FCSTD DOCUMENT  (FreeCAD 1.0R39109 (Git))
Label: splitflap
License: All rights reserved
LicenseURL: https://en.wikipedia.org/wiki/All_rights_reserved
objects: App::Link×18, App::FeaturePython×13, Assembly::AssemblyLink×1, Assembly::JointGroup×1, Assembly::AssemblyObject×1
EXTERNAL_REF file=front.FCStd obj=Body
EXTERNAL_REF file=sideLeft.FCStd obj=Body
EXTERNAL_REF file=sideMotor.FCStd obj=Body
EXTERNAL_REF file=bodySpacer.FCStd obj=Body
EXTERNAL_REF file=hardware/17HS13-0404D.FCStd obj=Part__Feature
EXTERNAL_REF file=motorSpacer.FCStd obj=Body
EXTERNAL_REF file=barrel/barrel.FCStd obj=Assembly
EXTERNAL_REF file=barrel/barrel.FCStd obj=Body
EXTERNAL_REF file=barrel/barrel.FCStd obj=Body001
EXTERNAL_REF file=barrel/barrel.FCStd obj=Body002
EXTERNAL_REF file=barrel/barrel.FCStd obj=Body003
EXTERNAL_REF file=barrel/barrel.FCStd obj=Body004
EXTERNAL_REF file=barrel/barrel.FCStd obj=Body007
EXTERNAL_REF file=barrel/barrel.FCStd obj=Body008
EXTERNAL_REF file=barrel/barrel.FCStd obj=Body009

FEATURE [App::Link] Body  label="Front"
  LinkPlacement = pos=(3.15e-14,-7,0) rot=(0,0,1;0rad)
  LinkedObject = -> <external front.FCStd>#Body
  Placement = pos=(3.15e-14,-7,0) rot=(0,0,1;0rad)
FEATURE [App::Link] Body006  label="LeftSide"
  LinkPlacement = pos=(36,-7,-80) rot=(0,0,1;0rad)
  LinkedObject = -> <external sideLeft.FCStd>#Body
  Placement = pos=(36,-7,-80) rot=(0,0,1;0rad)
FEATURE [App::Link] Body007  label="RightSide"
  LinkPlacement = pos=(-40,-7,-80) rot=(0,0,1;0rad)
  LinkedObject = -> <external sideMotor.FCStd>#Body
  Placement = pos=(-40,-7,-80) rot=(0,0,1;0rad)
FEATURE [App::Link] Body011  label="BodySpacerBottom"
  LinkPlacement = pos=(36,93,-75) rot=(0.57735,0.57735,-0.57735;4.18879rad)
  LinkedObject = -> <external bodySpacer.FCStd>#Body
  Placement = pos=(36,93,-75) rot=(0.57735,0.57735,-0.57735;4.18879rad)
FEATURE [App::Link] Body012  label="BodySpacerTop"
  LinkPlacement = pos=(36,88,70) rot=(0.57735,0.57735,-0.57735;4.18879rad)
  LinkedObject = -> <external bodySpacer.FCStd>#Body
  Placement = pos=(36,88,70) rot=(0.57735,0.57735,-0.57735;4.18879rad)
FEATURE [App::Link] _7HS13_0404D  label="17HS13-0404D"
  LinkPlacement = pos=(9,29,10) rot=(0.57735,0.57735,-0.57735;4.18879rad)
  LinkedObject = -> <external hardware/17HS13-0404D.FCStd>#Part__Feature
  Placement = pos=(9,29,10) rot=(0.57735,0.57735,-0.57735;4.18879rad)
FEATURE [App::Link] Body015  label="MotorSpacer"
  LinkPlacement = pos=(-36,13.5,-5.5) rot=(0.57735,0.57735,0.57735;2.0944rad)
  LinkedObject = -> <external motorSpacer.FCStd>#Body
  Placement = pos=(-36,13.5,-5.5) rot=(0.57735,0.57735,0.57735;2.0944rad)
FEATURE [App::Link] Body016  label="MotorSpacer001"
  LinkPlacement = pos=(-24,44.5,-5.5) rot=(0.57735,0.57735,-0.57735;4.18879rad)
  LinkedObject = -> <external motorSpacer.FCStd>#Body
  Placement = pos=(-24,44.5,-5.5) rot=(0.57735,0.57735,-0.57735;4.18879rad)
FEATURE [App::Link] Body017  label="MotorSpacer002"
  LinkPlacement = pos=(-24,44.5,25.5) rot=(-0.57735,-0.57735,0.57735;2.0944rad)
  LinkedObject = -> <external motorSpacer.FCStd>#Body
  Placement = pos=(-24,44.5,25.5) rot=(-0.57735,-0.57735,0.57735;2.0944rad)
FEATURE [App::Link] Body018  label="MotorSpacer003"
  LinkPlacement = pos=(-36,13.5,25.5) rot=(0.57735,0.57735,0.57735;2.0944rad)
  LinkedObject = -> <external motorSpacer.FCStd>#Body
  Placement = pos=(-36,13.5,25.5) rot=(0.57735,0.57735,0.57735;2.0944rad)
FEATURE [App::FeaturePython] GroundedJoint  # Assembly grounded joint (typed FeaturePython)
  ObjectToGround = -> Body
  Placement = pos=(3.15e-14,-7,0) rot=(0,0,1;0rad)
FEATURE [App::FeaturePython] Joint  label="FrontLeftTop"  # Assembly joint (typed FeaturePython)
  Activated = true
  AngleMax = 0
  AngleMin = 0
  Detach1 = false
  Detach2 = false
  Distance = 0
  Distance2 = 0
  EnableAngleMax = false
  EnableAngleMin = false
  EnableLengthMax = false
  EnableLengthMin = false
  JointType = 0 (Fixed)
  LengthMax = 0
  LengthMin = 0
  Offset2 = pos=(0,0,0) rot=(0,0,-1;1.5708rad)
  Placement1 = pos=(4,5,155) rot=(0.57735,0.57735,0.57735;2.0944rad)
  Placement2 = pos=(-36,5,75) rot=(0.57735,0.57735,0.57735;2.0944rad)
  Reference1 = -> Assembly [Body007.Edge325,Body007.Edge325]
  Reference2 = -> Assembly [Body.Edge70,Body.Edge70]
FEATURE [App::FeaturePython] Joint001  label="FrontRightTop001"  # Assembly joint (typed FeaturePython)
  Activated = true
  AngleMax = 0
  AngleMin = 0
  Detach1 = false
  Detach2 = false
  Distance = 0
  Distance2 = 0
  EnableAngleMax = false
  EnableAngleMin = false
  EnableLengthMax = false
  EnableLengthMin = false
  JointType = 0 (Fixed)
  LengthMax = 0
  LengthMin = 0
  Offset2 = pos=(0,0,0) rot=(0,0,-1;1.5708rad)
  Placement1 = pos=(-1.42e-14,5,155) rot=(0.57735,0.57735,0.57735;2.0944rad)
  Placement2 = pos=(36,5,75) rot=(0.57735,0.57735,0.57735;2.0944rad)
  Reference1 = -> Assembly [Body006.Edge101,Body006.Edge101]
  Reference2 = -> Assembly [Body.Edge65,Body.Edge65]
FEATURE [App::FeaturePython] Joint006  label="BodySpacerTop001"  # Assembly joint (typed FeaturePython)
  Activated = true
  AngleMax = 0
  AngleMin = 0
  Detach1 = false
  Detach2 = false
  Distance = 0
  Distance2 = 0
  EnableAngleMax = false
  EnableAngleMin = false
  EnableLengthMax = false
  EnableLengthMin = false
  JointType = 0 (Fixed)
  LengthMax = 0
  LengthMin = 0
  Placement1 = pos=(0,0,72) rot=(0,0,1;0rad)
  Placement2 = pos=(4,95,150) rot=(0.57735,0.57735,0.57735;2.0944rad)
  Reference1 = -> Assembly [Body012.Edge6,Body012.Edge6]
  Reference2 = -> Assembly [Body007.Edge326,Body007.Edge326]
FEATURE [App::FeaturePython] Joint007  label="BodySpacerBottom001"  # Assembly joint (typed FeaturePython)
  Activated = true
  AngleMax = 0
  AngleMin = 0
  Detach1 = false
  Detach2 = false
  Distance = 0
  Distance2 = 0
  EnableAngleMax = false
  EnableAngleMin = false
  EnableLengthMax = false
  EnableLengthMin = false
  JointType = 0 (Fixed)
  LengthMax = 0
  LengthMin = 0
  Placement1 = pos=(0,0,72) rot=(0,0,1;0rad)
  Placement2 = pos=(4,100,5) rot=(0.57735,0.57735,0.57735;2.0944rad)
  Reference1 = -> Assembly [Body011.Edge6,Body011.Edge6]
  Reference2 = -> Assembly [Body007.Edge328,Body007.Edge328]
FEATURE [App::FeaturePython] Joint010  label="FrontRightTop"  # Assembly joint (typed FeaturePython)
  Activated = true
  AngleMax = 0
  AngleMin = 0
  Detach1 = false
  Detach2 = false
  Distance = 0
  Distance2 = 0
  EnableAngleMax = false
  EnableAngleMin = false
  EnableLengthMax = false
  EnableLengthMin = false
  JointType = 0 (Fixed)
  LengthMax = 0
  LengthMin = 0
  Placement1 = pos=(-1.42e-14,5,155) rot=(0.57735,0.57735,0.57735;2.0944rad)
  Placement2 = pos=(36,5,75) rot=(0.707107,0,0.707107;3.14159rad)
  Reference1 = -> Assembly [Body006.Edge101,Body006.Edge101]
  Reference2 = -> Assembly [Body.Edge65,Body.Edge65]
FEATURE [App::Link] Body019  label="Body"
  LinkedObject = -> <external barrel/barrel.FCStd>#Body
FEATURE [App::Link] Body001  label="Spacer1"
  LinkPlacement = pos=(58,31.8049,3.72e-14) rot=(0.57735,0.57735,-0.57735;4.18879rad)
  LinkedObject = -> <external barrel/barrel.FCStd>#Body001
  Placement = pos=(58,31.8049,3.72e-14) rot=(0.57735,0.57735,-0.57735;4.18879rad)
FEATURE [App::Link] Body002  label="Spacer2"
  LinkPlacement = pos=(58,-1.99704,-31.7421) rot=(0.57735,0.57735,-0.57735;4.18879rad)
  LinkedObject = -> <external barrel/barrel.FCStd>#Body002
  Placement = pos=(58,-1.99704,-31.7421) rot=(0.57735,0.57735,-0.57735;4.18879rad)
FEATURE [App::Link] Body003  label="Spacer3"
  LinkPlacement = pos=(3,-31.8049,1.15e-14) rot=(0.57735,0.57735,0.57735;2.0944rad)
  LinkedObject = -> <external barrel/barrel.FCStd>#Body003
  Placement = pos=(3,-31.8049,1.15e-14) rot=(0.57735,0.57735,0.57735;2.0944rad)
FEATURE [App::Link] Body004  label="Spacer4"
  LinkPlacement = pos=(3,1.99704,31.7421) rot=(0.57735,0.57735,0.57735;2.0944rad)
  LinkedObject = -> <external barrel/barrel.FCStd>#Body004
  Placement = pos=(3,1.99704,31.7421) rot=(0.57735,0.57735,0.57735;2.0944rad)
FEATURE [App::Link] Body020  label="SideOpen"
  LinkPlacement = pos=(61,3.75e-14,5.47e-14) rot=(0,1,0;3.14159rad)
  LinkedObject = -> <external barrel/barrel.FCStd>#Body007
  Placement = pos=(61,3.75e-14,5.47e-14) rot=(0,1,0;3.14159rad)
FEATURE [App::Link] Body008  label="Flap2"
  LinkPlacement = pos=(30.5,-35.345,41.8018) rot=(1,0,0;4.64956rad)
  LinkedObject = -> <external barrel/barrel.FCStd>#Body008
  Placement = pos=(30.5,-35.345,41.8018) rot=(1,0,0;4.64956rad)
FEATURE [App::Link] Body009  label="Flap1"
  LinkPlacement = pos=(30.3278,-36.327,-41.8389) rot=(0,0.693562,0.720397;3.14159rad)
  LinkedObject = -> <external barrel/barrel.FCStd>#Body009
  Placement = pos=(30.3278,-36.327,-41.8389) rot=(0,0.693562,0.720397;3.14159rad)
FEATURE [Assembly::AssemblyLink] Assembly001  label="Barrel"
  Group = -> [Body019,Body001,Body002,Body003,Body004,Body020,Body008,Body009]
  LinkedObject = -> <external barrel/barrel.FCStd>#Assembly
  Origin = -> Origin001
  Placement = pos=(30.75,29,10) rot=(0,1,0;3.14159rad)
  Rigid = true
FEATURE [App::FeaturePython] Joint011  label="Cylindrical"  # Assembly joint (typed FeaturePython)
  Activated = true
  AngleMax = 0
  AngleMin = 0
  Detach1 = false
  Detach2 = false
  Distance = 0
  Distance2 = 0
  EnableAngleMax = false
  EnableAngleMin = false
  EnableLengthMax = false
  EnableLengthMin = false
  JointType = 2 (Cylindrical)
  LengthMax = 0
  LengthMin = 0
  Placement1 = pos=(6.75,-6.7e-15,6e-16) rot=(0.57735,0.57735,0.57735;2.0944rad)
  Placement2 = pos=(0,1.8e-15,3) rot=(0,1,0;3.14159rad)
  Reference1 = -> Assembly [Assembly001.Body019.Face2,Assembly001.Body019.Face2]
  Reference2 = -> Assembly [_7HS13_0404D.Face162,_7HS13_0404D.Edge2]
FEATURE [App::FeaturePython] Joint012  label="LeftMotorSpacer"  # Assembly joint (typed FeaturePython)
  Activated = true
  AngleMax = 0
  AngleMin = 0
  Detach1 = false
  Detach2 = false
  Distance = 0
  Distance2 = 0
  EnableAngleMax = false
  EnableAngleMin = false
  EnableLengthMax = false
  EnableLengthMin = false
  JointType = 0 (Fixed)
  LengthMax = 0
  LengthMin = 0
  Placement1 = pos=(0,-3.6e-15,12) rot=(0,0,1;0rad)
  Placement2 = pos=(4,51.5,105.5) rot=(0.57735,0.57735,0.57735;2.0944rad)
  Reference1 = -> Assembly [Body017.Edge6,Body017.Edge6]
  Reference2 = -> Assembly [Body007.Edge323,Body007.Edge323]
FEATURE [App::FeaturePython] Joint013  label="LeftMotorSpacer001"  # Assembly joint (typed FeaturePython)
  Activated = true
  AngleMax = 0
  AngleMin = 0
  Detach1 = false
  Detach2 = false
  Distance = 0
  Distance2 = 0
  EnableAngleMax = false
  EnableAngleMin = false
  EnableLengthMax = false
  EnableLengthMin = false
  JointType = 0 (Fixed)
  LengthMax = 0
  LengthMin = 0
  Placement2 = pos=(4,20.5,105.5) rot=(0.57735,0.57735,0.57735;2.0944rad)
  Reference1 = -> Assembly [Body018.Edge5,Body018.Edge5]
  Reference2 = -> Assembly [Body007.Edge324,Body007.Edge324]
FEATURE [App::FeaturePython] Joint014  label="LeftMotorSpacer002"  # Assembly joint (typed FeaturePython)
  Activated = true
  AngleMax = 0
  AngleMin = 0
  Detach1 = false
  Detach2 = false
  Distance = 0
  Distance2 = 0
  EnableAngleMax = false
  EnableAngleMin = false
  EnableLengthMax = false
  EnableLengthMin = false
  JointType = 0 (Fixed)
  LengthMax = 0
  LengthMin = 0
  Placement2 = pos=(4,20.5,74.5) rot=(0.57735,0.57735,0.57735;2.0944rad)
  Reference1 = -> Assembly [Body015.Edge5,Body015.Edge5]
  Reference2 = -> Assembly [Body007.Edge321,Body007.Edge321]
FEATURE [App::FeaturePython] Joint015  label="LeftMotorSpacer003"  # Assembly joint (typed FeaturePython)
  Activated = true
  AngleMax = 0
  AngleMin = 0
  Detach1 = false
  Detach2 = false
  Distance = 0
  Distance2 = 0
  EnableAngleMax = false
  EnableAngleMin = false
  EnableLengthMax = false
  EnableLengthMin = false
  JointType = 0 (Fixed)
  LengthMax = 0
  LengthMin = 0
  Placement1 = pos=(0,0,12) rot=(0,0,1;0rad)
  Placement2 = pos=(4,51.5,74.5) rot=(0.57735,0.57735,0.57735;2.0944rad)
  Reference1 = -> Assembly [Body016.Edge6,Body016.Edge6]
  Reference2 = -> Assembly [Body007.Edge322,Body007.Edge322]
FEATURE [App::FeaturePython] Joint016  label="MotorMotorSpacer"  # Assembly joint (typed FeaturePython)
  Activated = true
  AngleMax = 0
  AngleMin = 0
  Detach1 = false
  Detach2 = false
  Distance = 0
  Distance2 = 0
  EnableAngleMax = false
  EnableAngleMin = false
  EnableLengthMax = false
  EnableLengthMin = false
  JointType = 0 (Fixed)
  LengthMax = 0
  LengthMin = 0
  Placement1 = pos=(15.5,-15.5,33) rot=(1,0,0;3.14159rad)
  Reference1 = -> Assembly [_7HS13_0404D.Edge540,_7HS13_0404D.Edge540]
  Reference2 = -> Assembly [Body017.Pad.Edge5,Body017.Pad.Edge5]
FEATURE [App::FeaturePython] Joint017  label="MotorMotorSpacer001"  # Assembly joint (typed FeaturePython)
  Activated = true
  AngleMax = 0
  AngleMin = 0
  Detach1 = false
  Detach2 = false
  Distance = 0
  Distance2 = 0
  EnableAngleMax = false
  EnableAngleMin = false
  EnableLengthMax = false
  EnableLengthMin = false
  JointType = 0 (Fixed)
  LengthMax = 0
  LengthMin = 0
  Placement1 = pos=(-15.5,15.5,33) rot=(1,0,0;3.14159rad)
  Placement2 = pos=(0,0,12) rot=(0,0,1;0rad)
  Reference1 = -> Assembly [_7HS13_0404D.Edge538,_7HS13_0404D.Edge538]
  Reference2 = -> Assembly [Body015.Pad.Edge6,Body015.Pad.Edge6]
FEATURE [Assembly::JointGroup] Joints
  Group = -> [GroundedJoint,Joint,Joint001,Joint006,Joint007,Joint010,Joint011,Joint012,Joint013,Joint014,Joint015,Joint016,Joint017]
FEATURE [Assembly::AssemblyObject] Assembly
  Group = -> [Joints,Body,Body006,Body007,Body011,Body012,_7HS13_0404D,Body015,Body016,Body017,Body018,GroundedJoint,Joint,Joint001,Joint006,Joint007,Joint010,Assembly001,Joint011,Joint012,Joint013,Joint014,Joint015,Joint016,Joint017]
  Origin = -> Origin
  Type = Assembly

RESOLVED EXTERNAL PARTS (link-assembly join: the EXTERNAL_REF files above that resolve inside this repo's crawl, each included once):
---- part barrel/barrel.FCStd = doc fcstd_d6385020a1a2 ----
FCSTD DOCUMENT  (FreeCAD 1.0R39109 (Git))
Label: barrel
License: All rights reserved
LicenseURL: https://en.wikipedia.org/wiki/All_rights_reserved
objects: App::Link×10, App::FeaturePython×9, Assembly::JointGroup×1, Assembly::AssemblyObject×1
EXTERNAL_REF file=barrelMount.FCStd obj=Body
EXTERNAL_REF file=barrelSpacer.FCStd obj=Body
EXTERNAL_REF file=barrelSideOpen.FCStd obj=Body
EXTERNAL_REF file=../roundFlap.FCStd obj=Body

FEATURE [App::Link] Body
  LinkedObject = -> <external barrelMount.FCStd>#Body
FEATURE [App::FeaturePython] GroundedJoint  # Assembly grounded joint (typed FeaturePython)
  ObjectToGround = -> Body
FEATURE [App::Link] Body001  label="Spacer1"
  LinkPlacement = pos=(58,31.8049,3.72e-14) rot=(0.57735,0.57735,-0.57735;4.18879rad)
  LinkedObject = -> <external barrelSpacer.FCStd>#Body
  Placement = pos=(58,31.8049,3.72e-14) rot=(0.57735,0.57735,-0.57735;4.18879rad)
FEATURE [App::Link] Body002  label="Spacer2"
  LinkPlacement = pos=(58,-1.99704,-31.7421) rot=(0.57735,0.57735,-0.57735;4.18879rad)
  LinkedObject = -> <external barrelSpacer.FCStd>#Body
  Placement = pos=(58,-1.99704,-31.7421) rot=(0.57735,0.57735,-0.57735;4.18879rad)
FEATURE [App::Link] Body003  label="Spacer3"
  LinkPlacement = pos=(3,-31.8049,1.15e-14) rot=(0.57735,0.57735,0.57735;2.0944rad)
  LinkedObject = -> <external barrelSpacer.FCStd>#Body
  Placement = pos=(3,-31.8049,1.15e-14) rot=(0.57735,0.57735,0.57735;2.0944rad)
FEATURE [App::Link] Body004  label="Spacer4"
  LinkPlacement = pos=(3,1.99704,31.7421) rot=(0.57735,0.57735,0.57735;2.0944rad)
  LinkedObject = -> <external barrelSpacer.FCStd>#Body
  Placement = pos=(3,1.99704,31.7421) rot=(0.57735,0.57735,0.57735;2.0944rad)
FEATURE [App::Link] Body007  label="SideOpen"
  LinkPlacement = pos=(61,3.75e-14,5.47e-14) rot=(0,1,0;3.14159rad)
  LinkedObject = -> <external barrelSideOpen.FCStd>#Body
  Placement = pos=(61,3.75e-14,5.47e-14) rot=(0,1,0;3.14159rad)
FEATURE [App::Link] Body008  label="Flap2"
  LinkPlacement = pos=(30.5,-35.345,41.8018) rot=(1,0,0;4.64956rad)
  LinkedObject = -> <external ../roundFlap.FCStd>#Body
  Placement = pos=(30.5,-35.345,41.8018) rot=(1,0,0;4.64956rad)
FEATURE [App::Link] Body009  label="Flap1"
  LinkPlacement = pos=(30.3278,-36.327,-41.8389) rot=(0,0.693562,0.720397;3.14159rad)
  LinkedObject = -> <external ../roundFlap.FCStd>#Body
  Placement = pos=(30.3278,-36.327,-41.8389) rot=(0,0.693562,0.720397;3.14159rad)
FEATURE [App::Link] Body010  label="Unnamed"
FEATURE [App::Link] Body011  label="Unnamed"
FEATURE [App::FeaturePython] Joint  label="Fixed"  # Assembly joint (typed FeaturePython)
  Activated = true
  AngleMax = 0
  AngleMin = 0
  Detach1 = false
  Detach2 = false
  Distance = 0
  Distance2 = 0
  EnableAngleMax = false
  EnableAngleMin = false
  EnableLengthMax = false
  EnableLengthMin = false
  JointType = 0 (Fixed)
  LengthMax = 0
  LengthMin = 0
  Placement2 = pos=(3,-31.8049,1.15e-14) rot=(0.57735,0.57735,0.57735;2.0944rad)
  Reference1 = -> Assembly [Body003.Pad.Edge5,Body003.Pad.Edge5]
  Reference2 = -> Assembly [Body.Chamfer001.Edge234,Body.Chamfer001.Edge234]
FEATURE [App::FeaturePython] Joint008  label="Fixed001"  # Assembly joint (typed FeaturePython)
  Activated = true
  AngleMax = 0
  AngleMin = 0
  Detach1 = false
  Detach2 = false
  Distance = 0
  Distance2 = 0
  EnableAngleMax = false
  EnableAngleMin = false
  EnableLengthMax = false
  EnableLengthMin = false
  JointType = 0 (Fixed)
  LengthMax = 0
  LengthMin = 0
  Placement1 = pos=(0,0,55) rot=(0,0,1;0rad)
  Placement2 = pos=(3,31.8049,-1.78e-14) rot=(0.57735,0.57735,0.57735;2.0944rad)
  Reference1 = -> Assembly [Body001.Pad.Edge6,Body001.Pad.Edge6]
  Reference2 = -> Assembly [Body.Chamfer001.Edge190,Body.Chamfer001.Edge190]
FEATURE [App::FeaturePython] Joint009  label="Fixed002"  # Assembly joint (typed FeaturePython)
  Activated = true
  AngleMax = 0
  AngleMin = 0
  Detach1 = false
  Detach2 = false
  Distance = 0
  Distance2 = 0
  EnableAngleMax = false
  EnableAngleMin = false
  EnableLengthMax = false
  EnableLengthMin = false
  JointType = 0 (Fixed)
  LengthMax = 0
  LengthMin = 0
  Placement2 = pos=(3,1.99704,31.7421) rot=(0.57735,0.57735,0.57735;2.0944rad)
  Reference1 = -> Assembly [Body004.Pad.Edge5,Body004.Pad.Edge5]
  Reference2 = -> Assembly [Body.Chamfer001.Edge184,Body.Chamfer001.Edge184]
FEATURE [App::FeaturePython] Joint010  label="Fixed003"  # Assembly joint (typed FeaturePython)
  Activated = true
  AngleMax = 0
  AngleMin = 0
  Detach1 = false
  Detach2 = false
  Distance = 0
  Distance2 = 0
  EnableAngleMax = false
  EnableAngleMin = false
  EnableLengthMax = false
  EnableLengthMin = false
  JointType = 0 (Fixed)
  LengthMax = 0
  LengthMin = 0
  Placement1 = pos=(0,0,55) rot=(0,0,1;0rad)
  Placement2 = pos=(3,-1.99704,-31.7421) rot=(0.57735,0.57735,0.57735;2.0944rad)
  Reference1 = -> Assembly [Body002.Pad.Edge6,Body002.Pad.Edge6]
  Reference2 = -> Assembly [Body.Chamfer001.Edge240,Body.Chamfer001.Edge240]
FEATURE [App::FeaturePython] Joint011  label="Fixed004"  # Assembly joint (typed FeaturePython)
  Activated = true
  AngleMax = 0
  AngleMin = 0
  Detach1 = false
  Detach2 = false
  Distance = 0
  Distance2 = 0
  EnableAngleMax = false
  EnableAngleMin = false
  EnableLengthMax = false
  EnableLengthMin = false
  JointType = 0 (Fixed)
  LengthMax = 0
  LengthMin = 0
  Placement1 = pos=(3,-31.8049,6e-16) rot=(0.57735,0.57735,0.57735;2.0944rad)
  Placement2 = pos=(0,0,55) rot=(0,0,1;0rad)
  Reference1 = -> Assembly [Body007.Pocket001.Edge107,Body007.Pocket001.Edge107]
  Reference2 = -> Assembly [Body003.Pad.Edge6,Body003.Pad.Edge6]
FEATURE [App::FeaturePython] Joint012  label="Fixed005"  # Assembly joint (typed FeaturePython)
  Activated = true
  AngleMax = 0
  AngleMin = 0
  Detach1 = false
  Detach2 = false
  Distance = 0
  Distance2 = 0
  EnableAngleMax = false
  EnableAngleMin = false
  EnableLengthMax = false
  EnableLengthMin = false
  JointType = 0 (Fixed)
  LengthMax = 0
  LengthMin = 0
  Placement1 = pos=(3,31.8049,-2e-16) rot=(0.57735,0.57735,0.57735;2.0944rad)
  Reference1 = -> Assembly [Body007.Pocket001.Edge75,Body007.Pocket001.Edge75]
  Reference2 = -> Assembly [Body001.Pad.Edge5,Body001.Pad.Edge5]
FEATURE [App::FeaturePython] Joint013  label="Cylindrical"  # Assembly joint (typed FeaturePython)
  Activated = true
  AngleMax = 0
  AngleMin = 0
  Detach1 = false
  Detach2 = false
  Distance = 0
  Distance2 = 0
  EnableAngleMax = false
  EnableAngleMin = false
  EnableLengthMax = false
  EnableLengthMin = false
  JointType = 2 (Cylindrical)
  LengthMax = 0
  LengthMin = 0
  Placement1 = pos=(29,39.5,0.5) rot=(0.576441,-0.576441,-0.576441;2.0944rad)
  Placement2 = pos=(1.5,-37.3262,-2.34837) rot=(0.706932,-0.022216,0.706932;3.18602rad)
  Reference1 = -> Assembly [Body009.Face8,Body009.Face8]
  Reference2 = -> Assembly [Body.Face66,Body.Face66]
FEATURE [App::FeaturePython] Joint014  label="Cylindrical001"  # Assembly joint (typed FeaturePython)
  Activated = true
  AngleMax = 0
  AngleMin = 0
  Detach1 = false
  Detach2 = false
  Distance = 0
  Distance2 = 0
  EnableAngleMax = false
  EnableAngleMin = false
  EnableLengthMax = false
  EnableLengthMin = false
  JointType = 2 (Cylindrical)
  LengthMax = 0
  LengthMin = 0
  Placement1 = pos=(-29,39.5,0.5) rot=(-0.57735,0.57735,0.57735;4.18879rad)
  Placement2 = pos=(1.5,-37.3262,2.34837) rot=(0.706932,0.022216,0.706932;3.09717rad)
  Reference1 = -> Assembly [Body008.Face2,Body008.Face2]
  Reference2 = -> Assembly [Body.Face60,Body.Face60]
FEATURE [Assembly::JointGroup] Joints
  Group = -> [GroundedJoint,Joint,Joint008,Joint009,Joint010,Joint011,Joint012,Joint013,Joint014]
FEATURE [Assembly::AssemblyObject] Assembly
  Group = -> [Joints,Body,GroundedJoint,Body001,Body002,Body003,Body004,Body007,Body008,Body009,Joint,Joint008,Joint009,Joint010,Joint011,Joint012,Joint013,Joint014]
  Origin = -> Origin
  Type = Assembly
---- part bodySpacer.FCStd = doc fcstd_f0f4a3d15d17 ----
FCSTD DOCUMENT  (FreeCAD 1.0R39109 (Git))
Label: bodySpacer
License: All rights reserved
LicenseURL: https://en.wikipedia.org/wiki/All_rights_reserved
objects: Sketcher::SketchObject×1, PartDesign::Pad×1, PartDesign::Body×1
note: 6 computed .brp shape members not serialized (recipe doc carries the construction recipe); baked Part::Feature solids carry a one-line shape summary decoded from their .brp

FEATURE [Sketcher::SketchObject] Sketch
  ArcFitTolerance = 1e-06
  AttachmentSupport = -> [XY_Plane]
  FullyConstrained = true
  MakeInternals = false
  MapMode = 5
  sketch-geometry (2):
    g0: Circle CenterX=0 CenterY=0 CenterZ=0 NormalX=0 NormalY=0 NormalZ=1 AngleXU=0 Radius=1.5
    g1: Circle CenterX=0 CenterY=0 CenterZ=0 NormalX=0 NormalY=0 NormalZ=1 AngleXU=0 Radius=5
  constraints (4):
    c: Coincident(g0,g-1)
    c: Coincident(g1,g0)
    c: Diameter(g0) = 3
    c: Distance(g0,g1) = 3.5
FEATURE [PartDesign::Pad] Pad
  Direction = (0,0,1)
  Length = 72
  Length2 = 10
  Profile = -> Sketch
  ReferenceAxis = -> Sketch [N_Axis]
  Refine = true
  Suppressed = false
  Type = 0
FEATURE [PartDesign::Body] Body
  AllowCompound = false
  Group = -> [Sketch,Pad]
  Origin = -> Origin
  Tip = -> Pad
---- part front.FCStd = doc fcstd_f8b19ae0bcaa ----
FCSTD DOCUMENT  (FreeCAD 1.0R39109 (Git))
Label: front
License: All rights reserved
LicenseURL: https://en.wikipedia.org/wiki/All_rights_reserved
objects: Sketcher::SketchObject×3, PartDesign::Pad×2, PartDesign::Pocket×1, PartDesign::Fillet×1, PartDesign::Body×1
note: 19 computed .brp shape members not serialized (recipe doc carries the construction recipe); baked Part::Feature solids carry a one-line shape summary decoded from their .brp

FEATURE [Sketcher::SketchObject] Sketch
  ArcFitTolerance = 1e-06
  AttachmentSupport = -> [XZ_Plane]
  FullyConstrained = true
  MakeInternals = false
  MapMode = 5
  Placement = pos=(0,0,0) rot=(1,0,0;1.5708rad)
  sketch-geometry (21):
    g0: GeomPoint [constr] X=0 Y=0 Z=0
    g1: LineSegment StartX=-40 StartY=-80 StartZ=0 EndX=40 EndY=-80 EndZ=0
    g2: LineSegment StartX=40 StartY=-80 StartZ=0 EndX=40 EndY=80 EndZ=0
    g3: LineSegment StartX=40 StartY=80 StartZ=0 EndX=-40 EndY=80 EndZ=0
    g4: LineSegment StartX=-40 StartY=80 StartZ=0 EndX=-40 EndY=-80 EndZ=0
    g5: GeomPoint [constr] X=0 Y=0 Z=0
    g6: LineSegment StartX=-31.5 StartY=-15 StartZ=0 EndX=-28 EndY=-15 EndZ=0
    g7: LineSegment StartX=31.5 StartY=-15 StartZ=0 EndX=31.5 EndY=35 EndZ=0
    g8: LineSegment StartX=31.5 StartY=35 StartZ=0 EndX=28 EndY=35 EndZ=0
    g9: LineSegment StartX=-31.5 StartY=35 StartZ=0 EndX=-31.5 EndY=-15 EndZ=0
    g10: GeomPoint [constr] X=0 Y=10 Z=0
    g11: LineSegment StartX=-28 StartY=-60 StartZ=0 EndX=28 EndY=-60 EndZ=0
    g12: LineSegment StartX=28 StartY=-60 StartZ=0 EndX=28 EndY=-15 EndZ=0
    g13: LineSegment StartX=28 StartY=50 StartZ=0 EndX=-28 EndY=50 EndZ=0
    g14: LineSegment StartX=-28 StartY=50 StartZ=0 EndX=-28 EndY=35 EndZ=0
    g15: GeomPoint [constr] X=0 Y=-5 Z=0
    g16: LineSegment StartX=-28 StartY=35 StartZ=0 EndX=-31.5 EndY=35 EndZ=0
    g17: LineSegment StartX=-28 StartY=-15 StartZ=0 EndX=-28 EndY=-60 EndZ=0
    g18: LineSegment StartX=28 StartY=35 StartZ=0 EndX=28 EndY=50 EndZ=0
    g19: LineSegment StartX=28 StartY=-15 StartZ=0 EndX=31.5 EndY=-15 EndZ=0
    g20: LineSegment [constr] StartX=0 StartY=10 StartZ=0 EndX=-40 EndY=10 EndZ=0
  constraints (56):
    c: Coincident(g0,g-1)
    c: Coincident(g1,g2)
    c: Coincident(g2,g3)
    c: Coincident(g3,g4)
    c: Coincident(g4,g1)
    c: Horizontal(g1)
    c: Horizontal(g3)
    c: Vertical(g2)
    c: Vertical(g4)
    c: Symmetric(g3,g1,g5)
    c: Coincident(g5,g0)
    c: Coincident(g19,g7)
    c: Coincident(g7,g8)
    c: Coincident(g16,g9)
    c: Coincident(g9,g6)
    c: Horizontal(g6)
    c: Horizontal(g8)
    c: Vertical(g7)
    c: Vertical(g9)
    c: Symmetric(g8,g6,g10)
    c: PointOnObject(g10,g-2)
    c: DistanceX(g3,g3) = 80
    c: DistanceY(g2,g2) = 160
    c: Coincident(g11,g12)
    c: Coincident(g18,g13)
    c: Coincident(g13,g14)
    c: Coincident(g17,g11)
    c: Horizontal(g11)
    c: Horizontal(g13)
    c: Vertical(g12)
    c: Vertical(g14)
    c: Symmetric(g13,g11,g15)
    c: PointOnObject(g15,g-2)
    c: Distance(g1,g11) = 20
    c: Distance(g8,g13) = 15
    c: Distance(g12,g7) = 3.5
    c: Distance(g6,g8) = 50
    c: PointOnObject(g8,g18)
    c: Coincident(g14,g16)
    c: PointOnObject(g12,g19)
    c: PointOnObject(g18,g8)
    c: Coincident(g6,g17)
    c: PointOnObject(g19,g12)
    c: Horizontal(g6,g12)
    c: Vertical(g18)
    c: Horizontal(g19)
    c: Vertical(g17)
    c: Horizontal(g9,g14)
    c: Horizontal(g14,g8)
    c: Vertical(g14,g6)
    c: Vertical(g8,g12)
    c: Coincident(g20,g10)
    c: PointOnObject(g20,g4)
    c: Horizontal(g20)
    c: Distance(g1,g20) = 90
    c: Distance(g7,g9) = 63
FEATURE [PartDesign::Pad] Pad
  Direction = (0,-1,2e-16)
  Length = 3
  Length2 = 10
  Placement = pos=(0,0,0) rot=(1,0,0;1.5708rad)
  Profile = -> Sketch
  ReferenceAxis = -> Sketch [N_Axis]
  Refine = true
  Suppressed = false
  Type = 0
FEATURE [Sketcher::SketchObject] Sketch001
  ArcFitTolerance = 1e-06
  AttachmentSupport = -> [Pad]
  ExternalGeometry = -> [Pad]
  FullyConstrained = true
  MakeInternals = false
  MapMode = 5
  Placement = pos=(0,-4e-16,0) rot=(-1,0,0;1.5708rad)
  sketch-geometry (10):
    g0: LineSegment StartX=-36 StartY=70 StartZ=0 EndX=36 EndY=70 EndZ=0
    g1: LineSegment StartX=36 StartY=70 StartZ=0 EndX=36 EndY=80 EndZ=0
    g2: LineSegment StartX=36 StartY=80 StartZ=0 EndX=-36 EndY=80 EndZ=0
    g3: LineSegment StartX=-36 StartY=80 StartZ=0 EndX=-36 EndY=70 EndZ=0
    g4: GeomPoint [constr] X=0 Y=75 Z=0
    g5: LineSegment StartX=-36 StartY=-80 StartZ=0 EndX=36 EndY=-80 EndZ=0
    g6: LineSegment StartX=36 StartY=-80 StartZ=0 EndX=36 EndY=-70 EndZ=0
    g7: LineSegment StartX=36 StartY=-70 StartZ=0 EndX=-36 EndY=-70 EndZ=0
    g8: LineSegment StartX=-36 StartY=-70 StartZ=0 EndX=-36 EndY=-80 EndZ=0
    g9: GeomPoint [constr] X=0 Y=-75 Z=0
  constraints (26):
    c: Coincident(g0,g1)
    c: Coincident(g1,g2)
    c: Coincident(g2,g3)
    c: Coincident(g3,g0)
    c: Horizontal(g0)
    c: Horizontal(g2)
    c: Vertical(g1)
    c: Vertical(g3)
    c: Symmetric(g2,g0,g4)
    c: PointOnObject(g4,g-2)
    c: Coincident(g5,g6)
    c: Coincident(g6,g7)
    c: Coincident(g7,g8)
    c: Coincident(g8,g5)
    c: Horizontal(g5)
    c: Horizontal(g7)
    c: Vertical(g6)
    c: Vertical(g8)
    c: Symmetric(g7,g5,g9)
    c: PointOnObject(g9,g-2)
    c: PointOnObject(g5,g-4)
    c: PointOnObject(g1,g-3)
    c: Distance(g-3,g3) = 4
    c: DistanceY(g3,g3) = 10
    c: DistanceY(g8,g8) = 10
    c: Distance(g-4,g8) = 4
FEATURE [PartDesign::Pad] Pad001
  BaseFeature = -> Pad
  Direction = (0,1,2e-16)
  Length = 10
  Length2 = 10
  Placement = pos=(0,0,0) rot=(1,0,0;1.5708rad)
  Profile = -> Sketch001
  ReferenceAxis = -> Sketch001 [N_Axis]
  Refine = true
  Suppressed = false
  Type = 0
FEATURE [Sketcher::SketchObject] Sketch002
  ArcFitTolerance = 1e-06
  AttachmentSupport = -> [Pad001]
  ExternalGeometry = -> [Pad001]
  FullyConstrained = true
  MakeInternals = false
  MapMode = 5
  Placement = pos=(36,0,0) rot=(0.707107,0,0.707107;3.14159rad)
  sketch-geometry (2):
    g0: Circle CenterX=75 CenterY=-5 CenterZ=0 NormalX=0 NormalY=0 NormalZ=1 AngleXU=0 Radius=1.5
    g1: Circle CenterX=-75 CenterY=-5 CenterZ=0 NormalX=0 NormalY=0 NormalZ=1 AngleXU=0 Radius=1.5
  constraints (6):
    c: Diameter(g0) = 3
    c: Diameter(g1) = 3
    c: Distance(g1,g-3) = 5
    c: Distance(g0,g-4) = 5
    c: DistanceY(g-4,g0) = 5
    c: DistanceY(g-3,g1) = 5
FEATURE [PartDesign::Pocket] Pocket
  BaseFeature = -> Pad001
  Direction = (-1,0,2e-16)
  Length = 5
  Length2 = 5
  Midplane = true
  Placement = pos=(0,0,0) rot=(1,0,0;1.5708rad)
  Profile = -> Sketch002
  ReferenceAxis = -> Sketch002 [N_Axis]
  Refine = true
  Suppressed = false
  Type = 1
FEATURE [PartDesign::Fillet] Fillet
  Base = -> Pocket [Edge54,Edge61]
  BaseFeature = -> Pocket
  Placement = pos=(0,0,0) rot=(1,0,0;1.5708rad)
  Radius = 5
  Refine = true
  SupportTransform = false
  Suppressed = false
  UseAllEdges = false
FEATURE [PartDesign::Body] Body
  AllowCompound = false
  Group = -> [Sketch,Pad,Sketch001,Pad001,Sketch002,Pocket,Fillet]
  Origin = -> Origin
  Tip = -> Fillet
---- part motorSpacer.FCStd = doc fcstd_d5547a644473 ----
FCSTD DOCUMENT  (FreeCAD 1.0R39109 (Git))
Label: motorSpacer
License: All rights reserved
LicenseURL: https://en.wikipedia.org/wiki/All_rights_reserved
objects: Sketcher::SketchObject×1, PartDesign::Pad×1, PartDesign::Body×1
note: 6 computed .brp shape members not serialized (recipe doc carries the construction recipe); baked Part::Feature solids carry a one-line shape summary decoded from their .brp

FEATURE [Sketcher::SketchObject] Sketch
  ArcFitTolerance = 1e-06
  AttachmentSupport = -> [XY_Plane]
  FullyConstrained = true
  MakeInternals = false
  MapMode = 5
  sketch-geometry (2):
    g0: Circle CenterX=0 CenterY=0 CenterZ=0 NormalX=0 NormalY=0 NormalZ=1 AngleXU=0 Radius=1.6
    g1: Circle CenterX=0 CenterY=0 CenterZ=0 NormalX=0 NormalY=0 NormalZ=1 AngleXU=0 Radius=4.6
  constraints (4):
    c: Coincident(g0,g-1)
    c: Coincident(g1,g0)
    c: Diameter(g0) = 3.2
    c: Distance(g0,g1) = 3
FEATURE [PartDesign::Pad] Pad
  Direction = (0,0,1)
  Length = 12
  Length2 = 10
  Profile = -> Sketch
  ReferenceAxis = -> Sketch [N_Axis]
  Refine = true
  Suppressed = false
  Type = 0
FEATURE [PartDesign::Body] Body
  AllowCompound = false
  Group = -> [Sketch,Pad]
  Origin = -> Origin
  Tip = -> Pad
---- part sideLeft.FCStd = doc fcstd_d7bebf5dff4c ----
FCSTD DOCUMENT  (FreeCAD 1.0R39109 (Git))
Label: sideLeft
License: All rights reserved
LicenseURL: https://en.wikipedia.org/wiki/All_rights_reserved
objects: Sketcher::SketchObject×1, PartDesign::Pad×1, PartDesign::Fillet×1, PartDesign::Chamfer×1, PartDesign::Body×1
note: 12 computed .brp shape members not serialized (recipe doc carries the construction recipe); baked Part::Feature solids carry a one-line shape summary decoded from their .brp

FEATURE [Sketcher::SketchObject] Sketch
  ArcFitTolerance = 1e-06
  AttachmentSupport = -> [YZ_Plane]
  FullyConstrained = true
  MakeInternals = false
  MapMode = 5
  Placement = pos=(0,0,0) rot=(0.57735,0.57735,0.57735;2.0944rad)
  sketch-geometry (35):
    g0: LineSegment StartX=0 StartY=0 StartZ=0 EndX=105 EndY=0 EndZ=0
    g1: LineSegment StartX=0 StartY=160 StartZ=0 EndX=0 EndY=0 EndZ=0
    g2: Circle CenterX=5 CenterY=155 CenterZ=0 NormalX=0 NormalY=0 NormalZ=1 AngleXU=0 Radius=1.5
    g3: Circle CenterX=5 CenterY=5 CenterZ=0 NormalX=0 NormalY=0 NormalZ=1 AngleXU=0 Radius=1.5
    g4: Circle CenterX=100 CenterY=5 CenterZ=0 NormalX=0 NormalY=0 NormalZ=1 AngleXU=0 Radius=1.5
    g5: Circle CenterX=95 CenterY=150 CenterZ=0 NormalX=0 NormalY=0 NormalZ=1 AngleXU=0 Radius=1.5
    g6: LineSegment StartX=17.3087 StartY=10 StartZ=0 EndX=87.6913 EndY=10 EndZ=0
    g7: LineSegment StartX=95 StartY=17.3087 StartZ=0 EndX=95 EndY=142.691 EndZ=0
    g8: LineSegment StartX=87.6913 StartY=150 StartZ=0 EndX=17.3087 EndY=150 EndZ=0
    g9: LineSegment StartX=10 StartY=142.691 StartZ=0 EndX=10 EndY=17.3087 EndZ=0
    g10: ArcOfCircle CenterX=90 CenterY=145 CenterZ=0 NormalX=0 NormalY=0 NormalZ=1 AngleXU=0 Radius=15 StartAngle=8e-16 EndAngle=1.5708
    g11: LineSegment StartX=10 StartY=142.691 StartZ=0 EndX=46.706 EndY=80 EndZ=0
    g12: LineSegment StartX=95 StartY=17.3087 StartZ=0 EndX=58.294 EndY=80 EndZ=0
    g13: LineSegment StartX=87.6913 StartY=150 StartZ=0 EndX=52.5 EndY=89.8957 EndZ=0
    g14: LineSegment StartX=17.3087 StartY=10 StartZ=0 EndX=52.5 EndY=70.1043 EndZ=0
    g15: LineSegment StartX=0 StartY=160 StartZ=0 EndX=90 EndY=160 EndZ=0
    g16: LineSegment StartX=105 StartY=0 StartZ=0 EndX=105 EndY=145 EndZ=0
    g17: LineSegment [constr] StartX=90 StartY=160 StartZ=0 EndX=105 EndY=160 EndZ=0
    g18: LineSegment [constr] StartX=105 StartY=145 StartZ=0 EndX=105 EndY=160 EndZ=0
    g19: LineSegment StartX=46.706 StartY=80 StartZ=0 EndX=10 EndY=17.3087 EndZ=0
    g20: LineSegment StartX=52.5 StartY=89.8957 StartZ=0 EndX=17.3087 EndY=150 EndZ=0
    g21: LineSegment StartX=58.294 StartY=80 StartZ=0 EndX=95 EndY=142.691 EndZ=0
    g22: LineSegment StartX=52.5 StartY=70.1043 StartZ=0 EndX=87.6913 EndY=10 EndZ=0
    g23: LineSegment [constr] StartX=52.5 StartY=70.1043 StartZ=0 EndX=58.294 EndY=80 EndZ=0
    g24: LineSegment [constr] StartX=52.5 StartY=89.8957 StartZ=0 EndX=46.706 EndY=80 EndZ=0
    g25: LineSegment [constr] StartX=46.706 StartY=80 StartZ=0 EndX=52.5 EndY=70.1043 EndZ=0
    g26: LineSegment [constr] StartX=58.294 StartY=80 StartZ=0 EndX=52.5 EndY=89.8957 EndZ=0
    g27: LineSegment [constr] StartX=10 StartY=17.3087 StartZ=0 EndX=10 EndY=10 EndZ=0
    g28: LineSegment [constr] StartX=17.3087 StartY=10 StartZ=0 EndX=10 EndY=10 EndZ=0
    g29: LineSegment [constr] StartX=87.6913 StartY=10 StartZ=0 EndX=95 EndY=10 EndZ=0
    g30: LineSegment [constr] StartX=95 StartY=17.3087 StartZ=0 EndX=95 EndY=10 EndZ=0
    g31: LineSegment [constr] StartX=17.3087 StartY=150 StartZ=0 EndX=10 EndY=150 EndZ=0
    g32: LineSegment [constr] StartX=10 StartY=142.691 StartZ=0 EndX=10 EndY=150 EndZ=0
    g33: LineSegment [constr] StartX=87.6913 StartY=150 StartZ=0 EndX=95 EndY=150 EndZ=0
    g34: LineSegment [constr] StartX=95 StartY=142.691 StartZ=0 EndX=95 EndY=150 EndZ=0
  constraints (99):
    c: Coincident(g1,g0)
    c: Horizontal(g0)
    c: Vertical(g1)
    c: Coincident(g0,g-1)
    c: DistanceY(g1,g1) = 160
    c: DistanceX(g0,g0) = 105
    c: Diameter(g3) = 3
    c: Diameter(g4) = 3
    c: Diameter(g5) = 3
    c: Diameter(g2) = 3
    c: Distance(g0,g6) = 10
    c: Horizontal(g6)
    c: Horizontal(g8)
    c: Vertical(g9)
    c: Vertical(g7)
    c: Distance(g0,g7) = 10
    c: Coincident(g15,g1)
    c: Horizontal(g15)
    c: Coincident(g16,g0)
    c: Vertical(g16)
    c: Coincident(g15,g10)
    c: Coincident(g10,g16)
    c: Horizontal(g17)
    c: Coincident(g18,g10)
    c: Coincident(g18,g17)
    c: Coincident(g17,g10)
    c: Vertical(g18)
    c: Radius(g10) = 15
    c: DistanceX(g17,g17) = 15
    c: DistanceY(g18,g18) = 15
    c: Coincident(g21,g7)
    c: Coincident(g13,g8)
    c: Coincident(g20,g8)
    c: Coincident(g12,g7)
    c: Coincident(g22,g6)
    c: Coincident(g6,g14)
    c: Coincident(g19,g9)
    c: PointOnObject(g13,g20)
    c: PointOnObject(g12,g21)
    c: PointOnObject(g20,g13)
    c: PointOnObject(g14,g22)
    c: PointOnObject(g21,g12)
    c: Coincident(g11,g19)
    c: PointOnObject(g22,g14)
    c: Coincident(g11,g9)
    c: Distance(g15,g8) = 10
    c: Distance(g1,g9) = 10
    c: Parallel(g20,g11)
    c: Parallel(g12,g22)
    c: Parallel(g13,g21)
    c: Parallel(g19,g14)
    c: Coincident(g23,g14)
    c: Coincident(g23,g12)
    c: Coincident(g24,g13)
    c: Coincident(g24,g11)
    c: Coincident(g25,g11)
    c: Coincident(g25,g22)
    c: Coincident(g26,g21)
    c: Coincident(g26,g20)
    c: Coincident(g27,g9)
    c: Vertical(g27)
    c: Coincident(g28,g6)
    c: Horizontal(g28)
    c: Coincident(g29,g6)
    c: Horizontal(g29)
    c: Coincident(g30,g7)
    c: Vertical(g30)
    c: Coincident(g30,g29)
    c: Coincident(g27,g28)
    c: Coincident(g31,g8)
    c: Horizontal(g31)
    c: Coincident(g32,g9)
    c: Vertical(g32)
    c: Coincident(g31,g32)
    c: Coincident(g33,g8)
    c: Horizontal(g33)
    c: Coincident(g34,g7)
    c: Vertical(g34)
    c: Coincident(g33,g34)
    c: Parallel(g20,g26)
    c: Parallel(g26,g12)
    c: Parallel(g21,g24)
    c: Parallel(g24,g23)
    c: Parallel(g23,g19)
    c: Distance(g11,g20) = 10
    c: Distance(g13,g21) = 10
    c: Parallel(g22,g25)
    c: Distance(g4,g16) = 5
    c: Distance(g4,g0) = 5
    c: Distance(g3,g0) = 5
    c: Distance(g3,g1) = 5
    c: Distance(g2,g15) = 5
    c: Distance(g2,g1) = 5
    c: Distance(g5,g18) = 10
    c: Distance(g5,g17) = 10
    c: Equal(g31,g32)
    c: Equal(g29,g30)
    c: Equal(g28,g27)
    c: Equal(g34,g33)
FEATURE [PartDesign::Pad] Pad
  Direction = (1,0,0)
  Length = 4
  Length2 = 10
  Placement = pos=(0,0,0) rot=(1,1,1;2.0944rad)
  Profile = -> Sketch
  ReferenceAxis = -> Sketch [N_Axis]
  Refine = true
  Suppressed = false
  Type = 0
FEATURE [PartDesign::Fillet] Fillet
  Base = -> Pad [Edge35,Edge17,Edge44,Edge29,Edge38,Edge34,Edge25,Edge20,Edge26,Edge43,Edge16,Edge47]
  BaseFeature = -> Pad
  Placement = pos=(0,0,0) rot=(1,1,1;2.0944rad)
  Radius = 3
  Refine = true
  SupportTransform = false
  Suppressed = false
  UseAllEdges = false
FEATURE [PartDesign::Chamfer] Chamfer
  Angle = 45
  Base = -> Fillet [Edge49,Edge50,Edge52,Edge51]
  BaseFeature = -> Fillet
  ChamferType = 0
  FlipDirection = false
  Placement = pos=(0,0,0) rot=(1,1,1;2.0944rad)
  Refine = true
  Size = 2
  Size2 = 1
  SupportTransform = false
  Suppressed = false
  UseAllEdges = false
FEATURE [PartDesign::Body] Body
  AllowCompound = false
  Group = -> [Sketch,Pad,Fillet,Chamfer]
  Origin = -> Origin
  Tip = -> Chamfer
---- part sideMotor.FCStd = doc fcstd_1b755abe9b4c ----
FCSTD DOCUMENT  (FreeCAD 1.0R39109 (Git))
Label: sideMotor
License: All rights reserved
LicenseURL: https://en.wikipedia.org/wiki/All_rights_reserved
objects: Sketcher::SketchObject×4, PartDesign::Fillet×4, PartDesign::Chamfer×3, PartDesign::Pad×2, PartDesign::Pocket×2, PartDesign::Body×1
note: 42 computed .brp shape members not serialized (recipe doc carries the construction recipe); baked Part::Feature solids carry a one-line shape summary decoded from their .brp

FEATURE [Sketcher::SketchObject] Sketch
  ArcFitTolerance = 1e-06
  AttachmentSupport = -> [YZ_Plane]
  FullyConstrained = true
  MakeInternals = false
  MapMode = 5
  Placement = pos=(0,0,0) rot=(0.57735,0.57735,0.57735;2.0944rad)
  sketch-geometry (55):
    g0: LineSegment StartX=0 StartY=0 StartZ=0 EndX=105 EndY=0 EndZ=0
    g1: LineSegment StartX=0 StartY=160 StartZ=0 EndX=0 EndY=0 EndZ=0
    g2: Circle CenterX=36 CenterY=90 CenterZ=0 NormalX=0 NormalY=0 NormalZ=1 AngleXU=0 Radius=3.75
    g3: Circle CenterX=5 CenterY=155 CenterZ=0 NormalX=0 NormalY=0 NormalZ=1 AngleXU=0 Radius=1.5
    g4: Circle CenterX=95 CenterY=150 CenterZ=0 NormalX=0 NormalY=0 NormalZ=1 AngleXU=0 Radius=1.5
    g5: Circle CenterX=100 CenterY=5 CenterZ=0 NormalX=0 NormalY=0 NormalZ=1 AngleXU=0 Radius=1.5
    g6: Circle CenterX=5 CenterY=5 CenterZ=0 NormalX=0 NormalY=0 NormalZ=1 AngleXU=0 Radius=1.5
    g7: ArcOfCircle CenterX=10 CenterY=25 CenterZ=0 NormalX=0 NormalY=0 NormalZ=1 AngleXU=0 Radius=1.55 StartAngle=1.5708 EndAngle=4.71239
    g8: ArcOfCircle CenterX=30 CenterY=25 CenterZ=0 NormalX=0 NormalY=0 NormalZ=1 AngleXU=0 Radius=1.55 StartAngle=4.71239 EndAngle=7.85398
    g9: LineSegment StartX=10 StartY=26.55 StartZ=0 EndX=30 EndY=26.55 EndZ=0
    g10: LineSegment StartX=10 StartY=23.45 StartZ=0 EndX=30 EndY=23.45 EndZ=0
    g11: LineSegment [constr] StartX=20.5 StartY=74.5 StartZ=0 EndX=51.5 EndY=74.5 EndZ=0
    g12: LineSegment [constr] StartX=51.5 StartY=74.5 StartZ=0 EndX=51.5 EndY=105.5 EndZ=0
    g13: LineSegment [constr] StartX=51.5 StartY=105.5 StartZ=0 EndX=20.5 EndY=105.5 EndZ=0
    g14: LineSegment [constr] StartX=20.5 StartY=105.5 StartZ=0 EndX=20.5 EndY=74.5 EndZ=0
    g15: GeomPoint [constr] X=36 Y=90 Z=0
    g16: Circle CenterX=20.5 CenterY=105.5 CenterZ=0 NormalX=0 NormalY=0 NormalZ=1 AngleXU=0 Radius=1.55
    g17: Circle CenterX=51.5 CenterY=105.5 CenterZ=0 NormalX=0 NormalY=0 NormalZ=1 AngleXU=0 Radius=1.55
    g18: Circle CenterX=51.5 CenterY=74.5 CenterZ=0 NormalX=0 NormalY=0 NormalZ=1 AngleXU=0 Radius=1.55
    g19: Circle CenterX=20.5 CenterY=74.5 CenterZ=0 NormalX=0 NormalY=0 NormalZ=1 AngleXU=0 Radius=1.55
    g20: LineSegment StartX=0 StartY=160 StartZ=0 EndX=90 EndY=160 EndZ=0
    g21: LineSegment StartX=105 StartY=0 StartZ=0 EndX=105 EndY=145 EndZ=0
    g22: LineSegment [constr] StartX=90 StartY=160 StartZ=0 EndX=105 EndY=160 EndZ=0
    g23: LineSegment [constr] StartX=105 StartY=145 StartZ=0 EndX=105 EndY=160 EndZ=0
    g24: ArcOfCircle CenterX=90 CenterY=145 CenterZ=0 NormalX=0 NormalY=0 NormalZ=1 AngleXU=0 Radius=15 StartAngle=0 EndAngle=1.5708
    g25: LineSegment [constr] StartX=36 StartY=90 StartZ=0 EndX=100 EndY=5 EndZ=0
    g26: LineSegment [constr] StartX=36 StartY=90 StartZ=0 EndX=5 EndY=5 EndZ=0
    g27: ArcOfCircle CenterX=30 CenterY=25 CenterZ=0 NormalX=0 NormalY=0 NormalZ=1 AngleXU=0 Radius=7.5 StartAngle=4.71239 EndAngle=7.85398
    g28: LineSegment StartX=30 StartY=32.5 StartZ=0 EndX=20.3516 EndY=32.5 EndZ=0
    g29: LineSegment StartX=30 StartY=17.5 StartZ=0 EndX=14.881 EndY=17.5 EndZ=0
    g30: LineSegment StartX=61.4588 StartY=64.5 StartZ=0 EndX=95 EndY=64.5 EndZ=0
    g31: LineSegment StartX=95 StartY=64.5 StartZ=0 EndX=95 EndY=19.9531 EndZ=0
    g32: LineSegment StartX=32.0221 StartY=64.5 StartZ=0 EndX=20.3516 EndY=32.5 EndZ=0
    g33: LineSegment StartX=14.881 StartY=17.5 StartZ=0 EndX=12.1457 EndY=10 EndZ=0
    g34: LineSegment StartX=12.1457 StartY=10 StartZ=0 EndX=89.9765 EndY=10 EndZ=0
    g35: LineSegment [constr] StartX=105 StartY=64.5 StartZ=0 EndX=0 EndY=64.5 EndZ=0
    g36: LineSegment StartX=61.4588 StartY=64.5 StartZ=0 EndX=95 EndY=19.9531 EndZ=0
    g37: LineSegment StartX=89.9765 StartY=10 StartZ=0 EndX=48.9412 EndY=64.5 EndZ=0
    g38: LineSegment StartX=48.9412 StartY=64.5 StartZ=0 EndX=32.0221 EndY=64.5 EndZ=0
    g39: LineSegment [constr] StartX=30 StartY=25 StartZ=0 EndX=30 EndY=32.5 EndZ=0
    g40: LineSegment [constr] StartX=30 StartY=25 StartZ=0 EndX=30 EndY=17.5 EndZ=0
    g41: LineSegment [constr] StartX=36 StartY=90 StartZ=0 EndX=36 EndY=110 EndZ=0
    g42: LineSegment StartX=43.5 StartY=105 StartZ=0 EndX=43.5 EndY=115 EndZ=0
    g43: LineSegment StartX=43.5 StartY=115 StartZ=0 EndX=28.5 EndY=115 EndZ=0
    g44: LineSegment StartX=28.5 StartY=115 StartZ=0 EndX=28.5 EndY=105 EndZ=0
    g45: LineSegment StartX=28.5 StartY=105 StartZ=0 EndX=43.5 EndY=105 EndZ=0
    g46: GeomPoint [constr] X=36 Y=110 Z=0
    g47: LineSegment [constr] StartX=36 StartY=110 StartZ=0 EndX=5 EndY=155 EndZ=0
    g48: LineSegment StartX=14.516 StartY=150 StartZ=0 EndX=36.5605 EndY=118 EndZ=0
    g49: LineSegment StartX=14.516 StartY=150 StartZ=0 EndX=87.5 EndY=150 EndZ=0
    g50: LineSegment StartX=48.5 StartY=118 StartZ=0 EndX=36.5605 EndY=118 EndZ=0
    g51: LineSegment StartX=48.5 StartY=118 StartZ=0 EndX=53.5 EndY=130 EndZ=0
    g52: LineSegment StartX=53.5 StartY=130 StartZ=0 EndX=95 EndY=130 EndZ=0
    g53: LineSegment StartX=95 StartY=130 StartZ=0 EndX=95 EndY=142.5 EndZ=0
    g54: ArcOfCircle CenterX=95 CenterY=150 CenterZ=0 NormalX=0 NormalY=0 NormalZ=1 AngleXU=0 Radius=7.5 StartAngle=3.14159 EndAngle=4.71239
  constraints (148):
    c: Coincident(g1,g0)
    c: Horizontal(g0)
    c: Vertical(g1)
    c: Coincident(g0,g-1)
    c: Tangent(g7,g9) = 1.5708
    c: Tangent(g7,g10) = -1.5708
    c: Tangent(g8,g9) = 1.5708
    c: Tangent(g8,g10) = -1.5708
    c: Equal(g7,g8)
    c: Horizontal(g10)
    c: DistanceY(g-1,g2) = 90
    c: DistanceX(g0,g0) = 105
    c: DistanceY(g1,g1) = 160
    c: Diameter(g2) = 7.5
    c: Distance(g2,g1) = 36
    c: Diameter(g3) = 3
    c: Coincident(g11,g12)
    c: Coincident(g12,g13)
    c: Coincident(g13,g14)
    c: Coincident(g14,g11)
    c: Horizontal(g11)
    c: Horizontal(g13)
    c: Vertical(g12)
    c: Vertical(g14)
    c: Symmetric(g13,g11,g15)
    c: Coincident(g15,g2)
    c: DistanceY(g14,g14) = 31
    c: DistanceX(g13,g13) = 31
    c: Coincident(g16,g13)
    c: Diameter(g16) = 3.1
    c: Coincident(g17,g12)
    c: Coincident(g18,g11)
    c: Coincident(g19,g11)
    c: Equal(g16,g17)
    c: Equal(g17,g18)
    c: Equal(g18,g19)
    c: DistanceY(g-1,g7) = 25
    c: Distance(g10,g9) = 3.1
    c: DistanceX(g7,g8) = 20
    c: Distance(g7,g1) = 10
    c: Equal(g3,g4)
    c: Equal(g4,g5)
    c: Equal(g5,g6)
    c: Distance(g3,g1) = 5
    c: Distance(g6,g1) = 5
    c: Distance(g6,g0) = 5
    c: Distance(g5,g0) = 5
    c: Coincident(g20,g1)
    c: Horizontal(g20)
    c: Coincident(g21,g0)
    c: Vertical(g21)
    c: Coincident(g22,g20)
    c: Horizontal(g22)
    c: Coincident(g23,g21)
    c: Vertical(g23)
    c: Coincident(g22,g23)
    c: Coincident(g24,g20)
    c: Coincident(g24,g21)
    c: Distance(g5,g21) = 5
    c: Distance(g3,g20) = 5
    c: DistanceX(g22,g22) = 15
    c: DistanceY(g23,g23) = 15
    c: Distance(g4,g23) = 10
    c: Distance(g4,g22) = 10
    c: Distance(g24,g21) = 15
    c: Coincident(g25,g2)
    c: Coincident(g25,g5)
    c: Coincident(g26,g2)
    c: Coincident(g26,g6)
    c: Coincident(g27,g8)
    c: Coincident(g28,g27)
    c: Horizontal(g28)
    c: Coincident(g29,g27)
    c: Horizontal(g29)
    c: Horizontal(g30)
    c: Coincident(g31,g30)
    c: Vertical(g31)
    c: Coincident(g33,g29)
    c: Coincident(g34,g33)
    c: Horizontal(g34)
    c: Coincident(g32,g28)
    c: Parallel(g32,g26)
    c: Parallel(g33,g26)
    c: PointOnObject(g35,g1)
    c: Horizontal(g35)
    c: PointOnObject(g35,g21)
    c: Coincident(g36,g30)
    c: Coincident(g36,g31)
    c: Coincident(g37,g34)
    c: Coincident(g38,g37)
    c: Horizontal(g38)
    c: Coincident(g38,g32)
    c: PointOnObject(g37,g35)
    c: PointOnObject(g30,g35)
    c: Parallel(g36,g25)
    c: Parallel(g25,g37)
    c: Distance(g36,g25) = 5
    c: Distance(g21,g31) = 10
    c: Distance(g0,g34) = 10
    c: Radius(g27) = 7.5
    c: Distance(g26,g32) = 5
    c: Distance(g26,g33) = 5
    c: Distance(g37,g25) = 5
    c: Coincident(g39,g8)
    c: Coincident(g39,g27)
    c: Vertical(g39)
    c: Coincident(g40,g8)
    c: Coincident(g40,g27)
    c: Vertical(g40)
    c: Distance(g11,g35) = 10
    c: Coincident(g41,g2)
    c: Vertical(g41)
    c: Coincident(g42,g43)
    c: Coincident(g43,g44)
    c: Coincident(g44,g45)
    c: Coincident(g45,g42)
    c: Vertical(g42)
    c: Vertical(g44)
    c: Horizontal(g43)
    c: Horizontal(g45)
    c: Symmetric(g44,g42,g46)
    c: Coincident(g46,g41)
    c: DistanceX(g43,g43) = 15
    c: DistanceY(g44,g44) = 10
    c: DistanceY(g2,g41) = 20
    c: Coincident(g47,g41)
    c: Coincident(g47,g3)
    c: Coincident(g49,g48)
    c: Horizontal(g49)
    c: Parallel(g48,g47)
    c: Distance(g47,g48) = 5
    c: Horizontal(g50)
    c: Coincident(g50,g48)
    c: Distance(g43,g50) = 3
    c: Distance(g20,g49) = 10
    c: Coincident(g51,g50)
    c: Coincident(g52,g51)
    c: Horizontal(g52)
    c: DistanceX(g41,g50) = 12.5
    c: Distance(g52,g50) = 12
    c: DistanceX(g50,g51) = 5
    c: Coincident(g53,g52)
    c: Vertical(g53)
    c: Distance(g21,g53) = 10
    c: Coincident(g54,g4)
    c: Coincident(g54,g53)
    c: Coincident(g54,g49)
    c: Radius(g54) = 7.5
FEATURE [PartDesign::Pad] Pad
  Direction = (1,0,0)
  Length = 4
  Length2 = 10
  Placement = pos=(0,0,0) rot=(1,1,1;2.0944rad)
  Profile = -> Sketch
  ReferenceAxis = -> Sketch [N_Axis]
  Refine = true
  Suppressed = false
  Type = 0
FEATURE [Sketcher::SketchObject] Sketch001
  ArcFitTolerance = 1e-06
  FullyConstrained = true
  MakeInternals = false
  MapMode = 5
  Placement = pos=(-2.82e-14,0,0) rot=(0.57735,0.57735,-0.57735;4.18879rad)
  sketch-geometry (24):
    g0: LineSegment [constr] StartX=105 StartY=-96.6745 StartZ=0 EndX=50 EndY=-96.6745 EndZ=0
    g1: ArcOfCircle [constr] CenterX=50 CenterY=-110.026 CenterZ=0 NormalX=0 NormalY=0 NormalZ=1 AngleXU=0 Radius=13.3514 StartAngle=1.5708 EndAngle=3.06377
    g2: LineSegment [constr] StartX=50 StartY=-96.6745 StartZ=0 EndX=50 EndY=-110.026 EndZ=0
    g3: LineSegment [constr] StartX=36.689 StartY=-108.988 StartZ=0 EndX=36.6113 EndY=-109.985 EndZ=0
    g4: LineSegment [constr] StartX=52.5 StartY=-105.5 StartZ=0 EndX=44.75 EndY=-97.75 EndZ=0
    g5: LineSegment [constr] StartX=37 StartY=-90 StartZ=0 EndX=44.75 EndY=-97.75 EndZ=0
    g6: LineSegment StartX=34.1966 StartY=-108.794 StartZ=0 EndX=34.1189 EndY=-109.791 EndZ=0
    g7: ArcOfCircle CenterX=50 CenterY=-110.026 CenterZ=0 NormalX=0 NormalY=0 NormalZ=1 AngleXU=0 Radius=15.8514 StartAngle=1.5708 EndAngle=3.06377
    g8: LineSegment StartX=105 StartY=-94.1745 StartZ=0 EndX=50 EndY=-94.1745 EndZ=0
    g9: LineSegment StartX=105 StartY=-99.1745 StartZ=0 EndX=50 EndY=-99.1745 EndZ=0
    g10: ArcOfCircle CenterX=50 CenterY=-110.026 CenterZ=0 NormalX=0 NormalY=0 NormalZ=1 AngleXU=0 Radius=10.8514 StartAngle=1.5708 EndAngle=3.06377
    g11: LineSegment StartX=39.1815 StartY=-109.182 StartZ=0 EndX=39.1037 EndY=-110.179 EndZ=0
    g12: LineSegment StartX=105 StartY=-99.1745 StartZ=0 EndX=105 EndY=-94.1745 EndZ=0
    g13: LineSegment StartX=34.1189 StartY=-109.791 StartZ=0 EndX=39.1037 EndY=-110.179 EndZ=0
    g14: LineSegment [constr] StartX=37 StartY=-115 StartZ=0 EndX=37 EndY=-105 EndZ=0
    g15: LineSegment StartX=105 StartY=-124 StartZ=0 EndX=105 EndY=-120 EndZ=0
    g16: LineSegment StartX=105 StartY=-120 StartZ=0 EndX=75 EndY=-120 EndZ=0
    g17: LineSegment StartX=75 StartY=-124 StartZ=0 EndX=105 EndY=-124 EndZ=0
    g18: LineSegment [constr] StartX=105 StartY=-122 StartZ=0 EndX=45 EndY=-122 EndZ=0
    g19: LineSegment StartX=45 StartY=-126 StartZ=0 EndX=65 EndY=-126 EndZ=0
    g20: LineSegment StartX=65 StartY=-118 StartZ=0 EndX=45 EndY=-118 EndZ=0
    g21: LineSegment StartX=75 StartY=-124 StartZ=0 EndX=65 EndY=-126 EndZ=0
    g22: LineSegment StartX=75 StartY=-120 StartZ=0 EndX=65 EndY=-118 EndZ=0
    g23: LineSegment StartX=45 StartY=-118 StartZ=0 EndX=45 EndY=-126 EndZ=0
  constraints (66):
    c: Horizontal(g0)
    c: Coincident(g1,g0)
    c: Coincident(g2,g0)
    c: Vertical(g2)
    c: Coincident(g1,g2)
    c: PointOnObject(g0,g-3)
    c: Tangent(g3,g1) = -1.5708
    c: Coincident(g4,g-5)
    c: PointOnObject(g4,g1)
    c: Coincident(g5,g-6)
    c: Coincident(g5,g4)
    c: Equal(g4,g5)
    c: Parallel(g4,g5)
    c: Tangent(g6,g7) = -1.5708
    c: Tangent(g7,g8) = -1.5708
    c: Tangent(g9,g10) = -1.5708
    c: Tangent(g10,g11) = -1.5708
    c: Parallel(g9,g8)
    c: Parallel(g8,g0)
    c: Parallel(g11,g3)
    c: Parallel(g3,g6)
    c: Coincident(g12,g9)
    c: Coincident(g12,g8)
    c: Vertical(g12)
    c: Coincident(g13,g6)
    c: Coincident(g13,g11)
    c: PointOnObject(g3,g13)
    c: Distance(g8,g9) = 5
    c: Distance(g9,g0) = 2.5
    c: Coincident(g10,g1)
    c: Coincident(g7,g1)
    c: Perpendicular(g13,g3)
    c: PointOnObject(g9,g-3)
    c: Symmetric(g-7,g-7,g14)
    c: Symmetric(g-4,g-4,g14)
    c: PointOnObject(g14,g3)
    c: Distance(g14,g13) = 5
    c: DistanceX(g9,g9) = 55
    c: Coincident(g15,g16)
    c: Coincident(g17,g15)
    c: Vertical(g15)
    c: Horizontal(g16)
    c: Horizontal(g17)
    c: Symmetric(g15,g15,g18)
    c: Horizontal(g18)
    c: Horizontal(g19)
    c: Horizontal(g20)
    c: Coincident(g21,g17)
    c: Coincident(g21,g19)
    c: Coincident(g22,g16)
    c: Coincident(g22,g20)
    c: Coincident(g23,g20)
    c: Coincident(g23,g19)
    c: Vertical(g23)
    c: Distance(g16,g17) = 4
    c: Distance(g20,g19) = 8
    c: PointOnObject(g18,g23)
    c: DistanceX(g17,g17) = 30
    c: Equal(g16,g17)
    c: DistanceX(g21,g21) = 10
    c: DistanceX(g19,g19) = 20
    c: PointOnObject(g15,g-3)
    c: Equal(g20,g19)
    c: Distance(g19,g18) = 4
    c: Distance(g6,g6) = 1
    c: PointOnObject(g-8,g20)
FEATURE [Sketcher::SketchObject] Sketch002
  ArcFitTolerance = 1e-06
  ExternalGeometry = -> [Pad]
  FullyConstrained = true
  MakeInternals = false
  MapMode = 5
  Placement = pos=(-2.82e-14,0,0) rot=(0.57735,0.57735,-0.57735;4.18879rad)
  sketch-geometry (4):
    g0: Circle CenterX=51.5 CenterY=-105.5 CenterZ=0 NormalX=0 NormalY=0 NormalZ=1 AngleXU=0 Radius=3
    g1: Circle CenterX=20.5 CenterY=-105.5 CenterZ=0 NormalX=0 NormalY=0 NormalZ=1 AngleXU=0 Radius=3
    g2: Circle CenterX=20.5 CenterY=-74.5 CenterZ=0 NormalX=0 NormalY=0 NormalZ=1 AngleXU=0 Radius=3
    g3: Circle CenterX=51.5 CenterY=-74.5 CenterZ=0 NormalX=0 NormalY=0 NormalZ=1 AngleXU=0 Radius=3
  constraints (8):
    c: Diameter(g0) = 6
    c: Equal(g1,g2)
    c: Equal(g2,g3)
    c: Equal(g3,g0)
    c: Coincident(g-5,g1)
    c: Coincident(g-4,g2)
    c: Coincident(g-3,g3)
    c: Coincident(g-6,g0)
FEATURE [PartDesign::Pocket] Pocket
  BaseFeature = -> Pad
  Direction = (1,0,0)
  Length = 3
  Length2 = 5
  Placement = pos=(0,0,0) rot=(1,1,1;2.0944rad)
  Profile = -> Sketch002
  ReferenceAxis = -> Sketch002 [N_Axis]
  Refine = true
  Suppressed = false
  Type = 0
FEATURE [PartDesign::Chamfer] Chamfer001
  Angle = 45
  Base = -> Pocket [Edge40,Edge46,Edge39,Edge33]
  BaseFeature = -> Pocket
  ChamferType = 0
  FlipDirection = false
  Placement = pos=(0,0,0) rot=(1,1,1;2.0944rad)
  Refine = true
  Size = 0.5
  Size2 = 1
  SupportTransform = false
  Suppressed = false
  UseAllEdges = false
FEATURE [PartDesign::Pocket] Pocket001
  BaseFeature = -> Chamfer001
  Direction = (1,0,0)
  Length = 3
  Length2 = 5
  Placement = pos=(0,0,0) rot=(1,1,1;2.0944rad)
  Profile = -> Sketch001
  ReferenceAxis = -> Sketch001 [N_Axis]
  Refine = true
  Suppressed = false
  Type = 0
FEATURE [Sketcher::SketchObject] Sketch003
  ArcFitTolerance = 1e-06
  AttachmentSupport = -> [Pocket001]
  ExternalGeometry = -> [Pocket001]
  FullyConstrained = true
  MakeInternals = false
  MapMode = 5
  Placement = pos=(0,0,0) rot=(0.57735,0.57735,-0.57735;4.18879rad)
  sketch-geometry (22):
    g0: LineSegment StartX=50 StartY=-94.1745 StartZ=0 EndX=50 EndY=-96.6745 EndZ=0
    g1: LineSegment StartX=50 StartY=-96.6745 StartZ=0 EndX=57.5 EndY=-96.6745 EndZ=0
    g2: LineSegment StartX=57.5 StartY=-96.6745 StartZ=0 EndX=57.5 EndY=-94.1745 EndZ=0
    g3: LineSegment StartX=57.5 StartY=-94.1745 StartZ=0 EndX=50 EndY=-94.1745 EndZ=0
    g4: LineSegment StartX=73.75 StartY=-99.1745 StartZ=0 EndX=81.25 EndY=-99.1745 EndZ=0
    g5: LineSegment StartX=81.25 StartY=-99.1745 StartZ=0 EndX=81.25 EndY=-96.6745 EndZ=0
    g6: LineSegment StartX=81.25 StartY=-96.6745 StartZ=0 EndX=73.75 EndY=-96.6745 EndZ=0
    g7: LineSegment StartX=73.75 StartY=-96.6745 StartZ=0 EndX=73.75 EndY=-99.1745 EndZ=0
    g8: LineSegment StartX=105 StartY=-94.1745 StartZ=0 EndX=97.5 EndY=-94.1745 EndZ=0
    g9: LineSegment StartX=97.5 StartY=-94.1745 StartZ=0 EndX=97.5 EndY=-96.6745 EndZ=0
    g10: LineSegment StartX=97.5 StartY=-96.6745 StartZ=0 EndX=105 EndY=-96.6745 EndZ=0
    g11: LineSegment StartX=105 StartY=-96.6745 StartZ=0 EndX=105 EndY=-94.1745 EndZ=0
    g12: LineSegment StartX=105 StartY=-120 StartZ=0 EndX=97.5 EndY=-120 EndZ=0
    g13: LineSegment StartX=97.5 StartY=-120 StartZ=0 EndX=97.5 EndY=-121.75 EndZ=0
    g14: LineSegment StartX=97.5 StartY=-121.75 StartZ=0 EndX=105 EndY=-121.75 EndZ=0
    g15: LineSegment StartX=105 StartY=-121.75 StartZ=0 EndX=105 EndY=-120 EndZ=0
    g16: LineSegment StartX=75 StartY=-124 StartZ=0 EndX=82.5 EndY=-124 EndZ=0
    g17: LineSegment StartX=82.5 StartY=-124 StartZ=0 EndX=82.5 EndY=-122.25 EndZ=0
    g18: LineSegment StartX=82.5 StartY=-122.25 StartZ=0 EndX=75 EndY=-122.25 EndZ=0
    g19: LineSegment StartX=75 StartY=-122.25 StartZ=0 EndX=75 EndY=-124 EndZ=0
    g20: LineSegment [constr] StartX=57.5 StartY=-96.6745 StartZ=0 EndX=73.75 EndY=-96.6745 EndZ=0
    g21: LineSegment [constr] StartX=81.25 StartY=-96.6745 StartZ=0 EndX=97.5 EndY=-96.6745 EndZ=0
  constraints (60):
    c: Coincident(g0,g1)
    c: Coincident(g1,g2)
    c: Coincident(g2,g3)
    c: Coincident(g3,g0)
    c: Vertical(g0)
    c: Vertical(g2)
    c: Horizontal(g1)
    c: Horizontal(g3)
    c: Coincident(g0,g-3)
    c: Coincident(g4,g5)
    c: Coincident(g5,g6)
    c: Coincident(g6,g7)
    c: Coincident(g7,g4)
    c: Horizontal(g4)
    c: Horizontal(g6)
    c: Vertical(g5)
    c: Vertical(g7)
    c: Coincident(g8,g9)
    c: Coincident(g9,g10)
    c: Coincident(g10,g11)
    c: Coincident(g11,g8)
    c: Horizontal(g8)
    c: Horizontal(g10)
    c: Vertical(g9)
    c: Vertical(g11)
    c: Coincident(g8,g-3)
    c: Coincident(g12,g13)
    c: Coincident(g13,g14)
    c: Coincident(g14,g15)
    c: Coincident(g15,g12)
    c: Horizontal(g12)
    c: Horizontal(g14)
    c: Vertical(g13)
    c: Vertical(g15)
    c: Coincident(g12,g-5)
    c: Coincident(g16,g17)
    c: Coincident(g17,g18)
    c: Coincident(g18,g19)
    c: Coincident(g19,g16)
    c: Horizontal(g16)
    c: Horizontal(g18)
    c: Vertical(g17)
    c: Vertical(g19)
    c: Coincident(g16,g-6)
    c: Equal(g2,g7)
    c: Equal(g7,g9)
    c: Equal(g17,g13)
    c: DistanceY(g11,g11) = 2.5
    c: DistanceX(g3,g3) = 7.5
    c: DistanceX(g4,g4) = 7.5
    c: DistanceX(g12,g12) = 7.5
    c: DistanceX(g16,g16) = 7.5
    c: DistanceY(g15,g15) = 1.75
    c: DistanceX(g8,g8) = 7.5
    c: Coincident(g20,g1)
    c: Coincident(g20,g6)
    c: Coincident(g21,g5)
    c: Coincident(g21,g9)
    c: Horizontal(g21)
    c: Equal(g21,g20)
FEATURE [PartDesign::Pad] Pad001
  BaseFeature = -> Pocket001
  Direction = (-1,0,0)
  Length = 1
  Length2 = 10
  Placement = pos=(0,0,0) rot=(1,1,1;2.0944rad)
  Profile = -> Sketch003
  ReferenceAxis = -> Sketch003 [N_Axis]
  Refine = true
  Reversed = true
  Suppressed = false
  Type = 0
FEATURE [PartDesign::Chamfer] Chamfer002
  Angle = 45
  Base = -> Pad001 [Edge168,Edge144,Edge172,Edge90,Edge123]
  BaseFeature = -> Pad001
  ChamferType = 1
  FlipDirection = false
  Placement = pos=(0,0,0) rot=(1,1,1;2.0944rad)
  Refine = true
  Size = 0.8
  Size2 = 1.5
  SupportTransform = false
  Suppressed = false
  UseAllEdges = false
FEATURE [PartDesign::Fillet] Fillet
  Base = -> Chamfer002 [Edge196,Edge198,Edge197,Edge199]
  BaseFeature = -> Chamfer002
  Placement = pos=(0,0,0) rot=(1,1,1;2.0944rad)
  Radius = 1.5
  Refine = true
  SupportTransform = false
  Suppressed = false
  UseAllEdges = false
FEATURE [PartDesign::Fillet] Fillet001
  Base = -> Fillet [Edge185,Edge190,Edge120,Edge157,Edge94,Edge132,Edge108,Edge114,Edge97,Edge136]
  BaseFeature = -> Fillet
  Placement = pos=(0,0,0) rot=(1,1,1;2.0944rad)
  Radius = 1
  Refine = true
  SupportTransform = false
  Suppressed = false
  UseAllEdges = false
FEATURE [PartDesign::Fillet] Fillet002
  Base = -> Fillet001 [Edge168,Edge173,Edge152,Edge150,Edge235,Edge223,Edge225,Edge227]
  BaseFeature = -> Fillet001
  Placement = pos=(0,0,0) rot=(1,1,1;2.0944rad)
  Radius = 5
  Refine = true
  SupportTransform = false
  Suppressed = false
  UseAllEdges = false
FEATURE [PartDesign::Fillet] Fillet003
  Base = -> Fillet002 [Edge282,Edge268,Edge264,Edge286,Edge260,Edge98,Edge109,Edge105]
  BaseFeature = -> Fillet002
  Placement = pos=(0,0,0) rot=(1,1,1;2.0944rad)
  Radius = 2.5
  Refine = true
  SupportTransform = false
  Suppressed = false
  UseAllEdges = false
FEATURE [PartDesign::Chamfer] Chamfer003
  Angle = 45
  Base = -> Fillet003 [Edge66,Edge75,Edge74,Edge72,Edge73]
  BaseFeature = -> Fillet003
  ChamferType = 0
  FlipDirection = false
  Placement = pos=(0,0,0) rot=(1,1,1;2.0944rad)
  Refine = true
  Size = 2
  Size2 = 1
  SupportTransform = false
  Suppressed = false
  UseAllEdges = false
FEATURE [PartDesign::Body] Body
  AllowCompound = false
  Group = -> [Sketch,Pad,Sketch001,Sketch002,Pocket,Chamfer001,Pocket001,Sketch003,Pad001,Chamfer002,Fillet,Fillet001,Fillet002,Fillet003,Chamfer003]
  Origin = -> Origin
  Tip = -> Chamfer003
